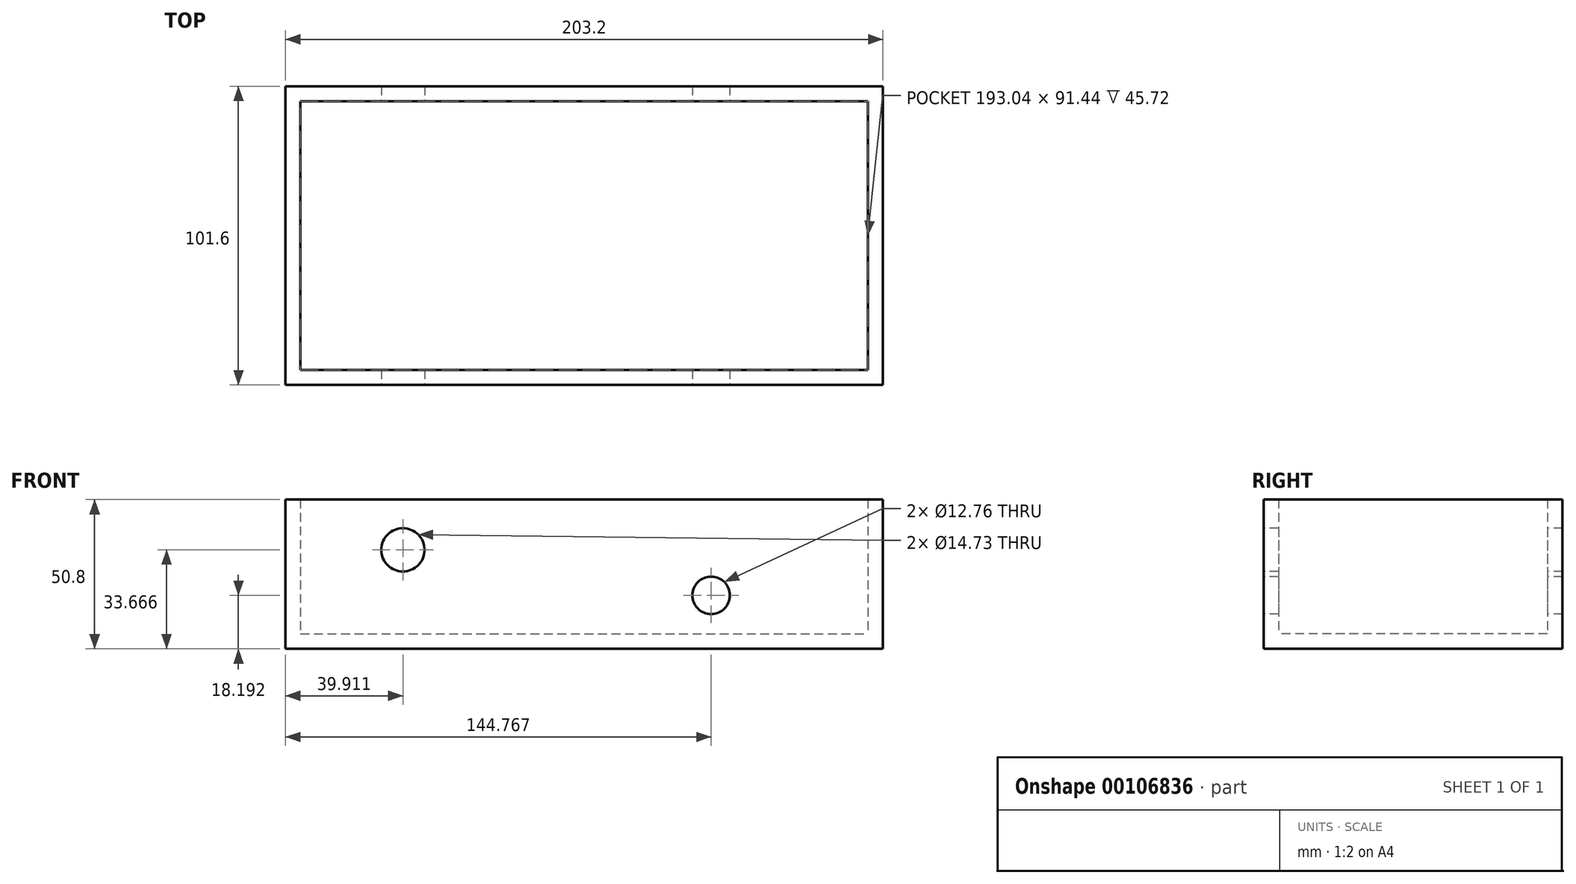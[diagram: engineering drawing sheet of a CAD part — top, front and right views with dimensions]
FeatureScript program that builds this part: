
annotation { "Feature Type Name" : "Feature", "Feature Type Description" : "" }
export const myFeature = defineFeature(function(context is Context, id is Id, definition is map)
    precondition{}
    {
        {
            var Q0;
            Q0=qCreatedBy(makeId("Top.planeOp"),FACE);
            var sketch = newSketch(context, id + "F0", { "sketchPlane" : qUnion([Q0])});
            skLineSegment(sketch, "E0.bottom", {"start": v(-101.6, 50.8) * mm, "end": v(101.6, 50.8) * mm});
            skLineSegment(sketch, "E0.top", {"start": v(-101.6, -50.8) * mm, "end": v(101.6, -50.8) * mm});
            skLineSegment(sketch, "E0.left", {"start": v(-101.6, 50.8) * mm, "end": v(-101.6, -50.8) * mm});
            skLineSegment(sketch, "E0.right", {"start": v(101.6, 50.8) * mm, "end": v(101.6, -50.8) * mm});
            skSolve(sketch);
        }
        {
            var Q0;
            Q0=makeQuery(id+"F0.imprint","IMPRINT",FACE,{"disambiguationData":[TD([[makeQuery(id+"F0.imprint","IMPRINT",EDGE,{"derivedFrom":sQuery(id+"F0.wireOp",EDGE,"E0.bottom")}),-1.0]])]});
            extrude(context, id + "F1", {"entities" : qUnion([Q0]), "depth" : 25.4 * mm, "hasSecondDirection" : true, "secondDirectionOppositeDirection" : true, "secondDirectionDepth" : 25.4 * mm});
        }
        {
            var Q0;
            Q0=makeQuery(id+"F1.opExtrude","CAP_FACE",FACE,{"disambiguationData":[OSD([sQuery(id+"F0.wireOp",EDGE,"E0.bottom"),sQuery(id+"F0.wireOp",EDGE,"E0.top"),sQuery(id+"F0.wireOp",EDGE,"E0.left"),sQuery(id+"F0.wireOp",EDGE,"E0.right")])],"isStart":false});
            shell(context, id + "F2", {"entities" : qUnion([Q0]), "thickness" : 5.08 * mm});
        }
        {
            var Q0;
            Q0=makeQuery(id+"F1.opExtrude","SWEPT_FACE",FACE,{"disambiguationData":[OSD([sQuery(id+"F0.wireOp",EDGE,"E0.top")])]});
            var sketch = newSketch(context, id + "F3", { "sketchPlane" : qUnion([Q0])});
            skCircle(sketch, "E1", {"center": v(-61.69, 8.27) * mm, "radius": 7.36 * mm});
            skCircle(sketch, "E2", {"center": v(43.17, -7.2) * mm, "radius": 6.38 * mm});
            skSolve(sketch);
        }
        {
            var Q0;
            Q0=makeQuery(id+"F3.imprint","IMPRINT",FACE,{"disambiguationData":[TD([[makeQuery(id+"F3.imprint","IMPRINT",EDGE,{"derivedFrom":sQuery(id+"F3.wireOp",EDGE,"E1")}),1.0]])]});
            var Q1;
            Q1=makeQuery(id+"F3.imprint","IMPRINT",FACE,{"disambiguationData":[TD([[makeQuery(id+"F3.imprint","IMPRINT",EDGE,{"derivedFrom":sQuery(id+"F3.wireOp",EDGE,"E2")}),1.0]])]});
            extrude(context, id + "F4", {"entities" : qUnion([Q0, Q1]), "operationType" : NewBodyOperationType.REMOVE, "endBound" : BoundingType.THROUGH_ALL, "oppositeDirection" : true, "depth" : 25.4 * mm});
        }
    });
